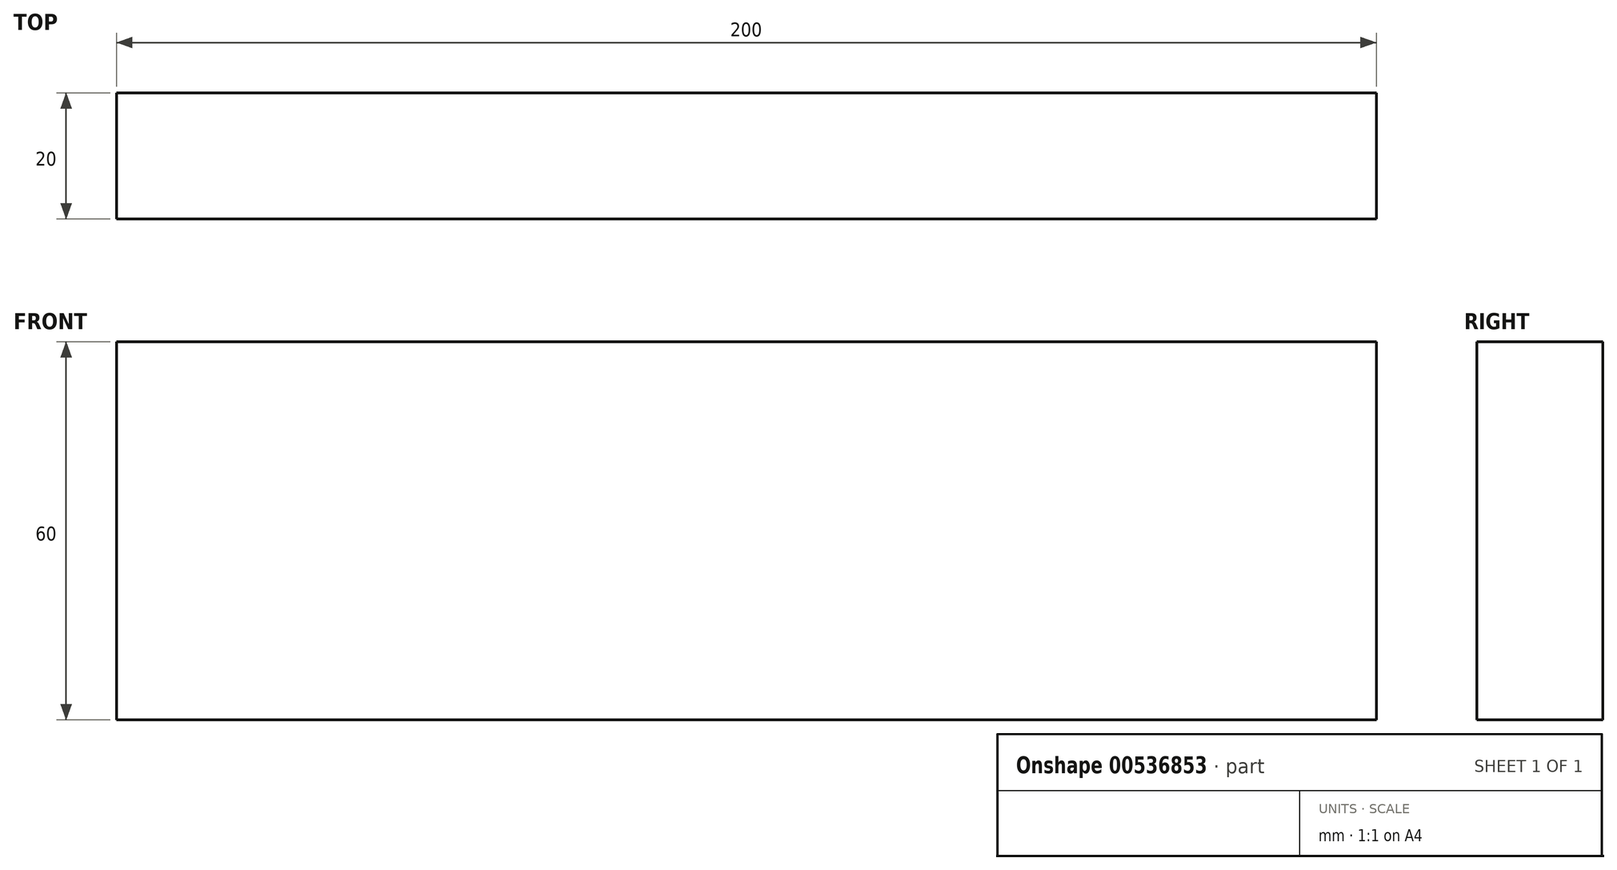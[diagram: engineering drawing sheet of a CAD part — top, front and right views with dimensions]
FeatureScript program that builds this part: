
annotation { "Feature Type Name" : "Feature", "Feature Type Description" : "" }
export const myFeature = defineFeature(function(context is Context, id is Id, definition is map)
    precondition{}
    {
        {
            var Q0;
            Q0=qCreatedBy(makeId("Front.planeOp"),FACE);
            var sketch = newSketch(context, id + "F0", { "sketchPlane" : qUnion([Q0])});
            skLineSegment(sketch, "E0.bottom", {"start": v(100, -30) * mm, "end": v(-100, -30) * mm});
            skLineSegment(sketch, "E0.top", {"start": v(100, 30) * mm, "end": v(-100, 30) * mm});
            skLineSegment(sketch, "E0.left", {"start": v(100, -30) * mm, "end": v(100, 30) * mm});
            skLineSegment(sketch, "E0.right", {"start": v(-100, -30) * mm, "end": v(-100, 30) * mm});
            skPoint(sketch, "E0.middle", {"position": v(0, 0) * mm});
            skSolve(sketch);
        }
        {
            var Q0;
            Q0 = qSketchRegion(id + "F0", true);
            extrude(context, id + "F1", {"entities" : qUnion([Q0]), "endBound" : BoundingType.SYMMETRIC, "depth" : 20 * mm, "offsetDistance" : 25 * mm});
        }
    });
